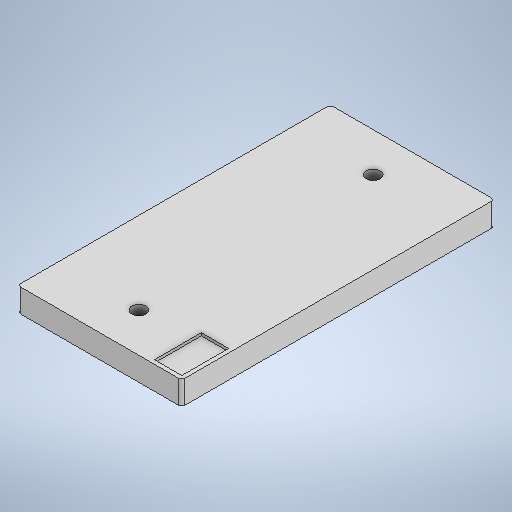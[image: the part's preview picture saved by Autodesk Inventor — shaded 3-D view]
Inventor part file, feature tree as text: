
AUTODESK INVENTOR PART (.ipt)
format: ipt  version: 2025 (Build 290162000, 162)  size: 246,272 bytes
history: native  units: in
note: dims shown in document units (in); Inventor stores cm internally (conversion verified against a paired STEP export)
features: sketch x3, extrude x2, hole x1, fillet x1
ambient origin geometry x8: Origin, YZ Plane, XZ Plane, XY Plane, X Axis, Y Axis, Z Axis, Center Point
bodies: Solid1 (feature_tree)
feature tree (7):
  extrude  "Extrusion1"  Depth=15.748in
  hole  "Hole1"  [1 undecoded]
  extrude  "Extrusion2"  Depth=15.748in
  fillet  "Fillet1"  Radius=5.9055in
  sketch  "Sketch1"  dims[d0=8.2677in d1=15.748in]
  sketch  "Sketch2"  dims[d2=1.1811in d3=0.0in d4=0.7087in]
  sketch  "Sketch3"  dims[d5=0.7087in d6=5.9055in d7=5.9055in d8=0.0039in d9=0.2341in d10=0.7087in d11=0.9449in d12=90.0deg d13=0.315in d14=0.8108in d15=1.378in d16=2.3622in d17=0.1969in d19=0.1969in d20=0.1378in d21=0.0in d22=0.1575in d23=15.748in]
note: 1 required parameter value undecoded (feature->parameter linkage not recoverable at this tier; creation-order binding heuristic only, values carry confidence <= 0.55)
